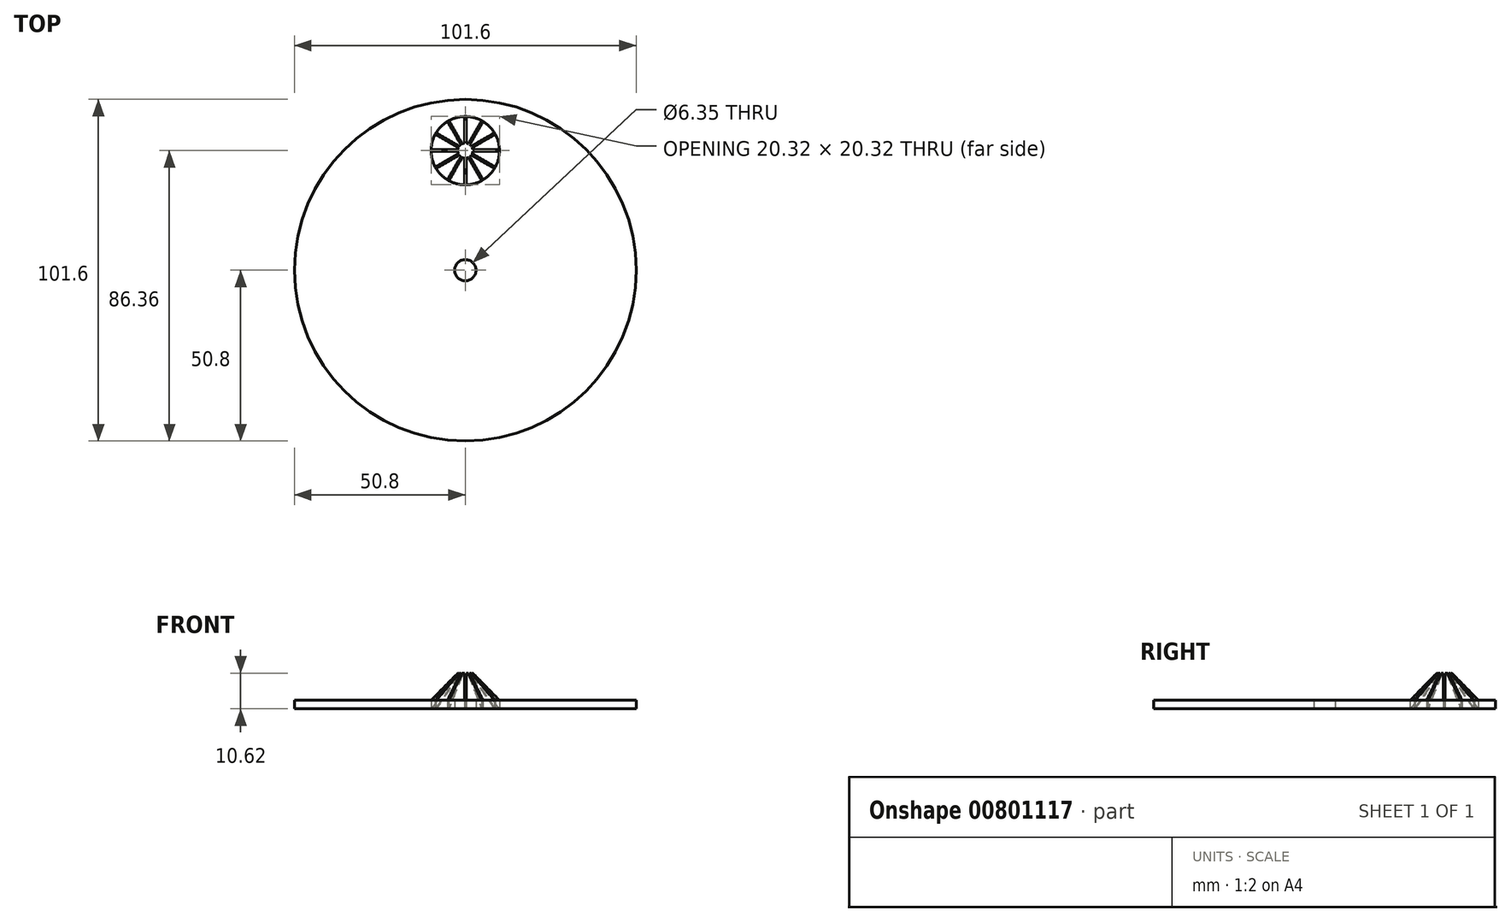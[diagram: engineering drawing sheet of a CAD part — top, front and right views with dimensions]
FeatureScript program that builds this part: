
annotation { "Feature Type Name" : "Feature", "Feature Type Description" : "" }
export const myFeature = defineFeature(function(context is Context, id is Id, definition is map)
    precondition{}
    {
        {
            var Q0;
            Q0=qCreatedBy(makeId("Top.planeOp"),FACE);
            var sketch = newSketch(context, id + "F0", { "sketchPlane" : qUnion([Q0])});
            skCircle(sketch, "E0", {"center": v(0, 0) * mm, "radius": 50.8 * mm});
            skCircle(sketch, "E1", {"center": v(0, 0) * mm, "radius": 3.18 * mm});
            skSolve(sketch);
        }
        {
            var Q0;
            Q0 = qSketchRegion(id + "F0", true);
            extrude(context, id + "F1", {"entities" : qUnion([Q0]), "depth" : 2.54 * mm, "offsetDistance" : 25.4 * mm});
        }
        {
            var Q0;
            Q0=makeQuery(id+"F1.opExtrude","CAP_FACE",FACE,{"disambiguationData":[OSD([sQuery(id+"F0.wireOp",EDGE,"E0"),sQuery(id+"F0.wireOp",EDGE,"E1")])],"isStart":false});
            var sketch = newSketch(context, id + "F2", { "sketchPlane" : qUnion([Q0])});
            skLineSegment(sketch, "E2", {"start": v(0, 0) * mm, "end": v(0, 35.56) * mm, "construction": true});
            skCircle(sketch, "E3", {"center": v(0, 35.56) * mm, "radius": 10.16 * mm});
            skSolve(sketch);
        }
        {
            var Q0;
            Q0=makeQuery(id+"F2.imprint","IMPRINT",FACE,{"disambiguationData":[TD([[makeQuery(id+"F2.imprint","IMPRINT",EDGE,{"derivedFrom":sQuery(id+"F2.wireOp",EDGE,"E3")}),1.0]])]});
            var Q1;
            Q1=sQuery(id+"F2.wireOp",EDGE,"E3");
            extrude(context, id + "F3", {"entities" : qUnion([Q0]), "operationType" : NewBodyOperationType.REMOVE, "surfaceEntities" : qUnion([Q1]), "oppositeDirection" : true, "depth" : 25.4 * mm, "offsetDistance" : 25.4 * mm});
        }
        {
            var Q0;
            Q0=qCreatedBy(makeId("Right.planeOp"),FACE);
            var sketch = newSketch(context, id + "F4", { "sketchPlane" : qUnion([Q0])});
            skLineSegment(sketch, "E4", {"start": v(45.72, 2.54) * mm, "end": v(37.8, 10.62) * mm});
            skLineSegment(sketch, "E5", {"start": v(37.8, 10.62) * mm, "end": v(37.8, 10) * mm});
            skLineSegment(sketch, "E6", {"start": v(37.8, 10) * mm, "end": v(45.72, 0) * mm});
            skLineSegment(sketch, "E7", {"start": v(45.72, 2.54) * mm, "end": v(45.72, 0) * mm});
            skSolve(sketch);
        }
        {
            var Q0;
            Q0=makeQuery(id+"F4.imprint","IMPRINT",FACE,{"disambiguationData":[TD([[makeQuery(id+"F4.imprint","IMPRINT",EDGE,{"derivedFrom":sQuery(id+"F4.wireOp",EDGE,"E4")}),1.0]])]});
            var Q1;
            Q1=sQuery(id+"F2.wireOp",EDGE,"E3");
            revolve(context, id + "F5", {"operationType" : NewBodyOperationType.ADD, "surfaceOperationType" : NewSurfaceOperationType.NEW, "entities" : qUnion([Q0]), "axis" : qUnion([Q1]), "revolveType" : RevolveType.FULL});
        }
        {
            var Q0;
            Q0=makeQuery(id+"F1.opExtrude","CAP_FACE",FACE,{"disambiguationData":[OSD([sQuery(id+"F0.wireOp",EDGE,"E0"),sQuery(id+"F0.wireOp",EDGE,"E1")])],"isStart":true});
            var sketch = newSketch(context, id + "F6", { "sketchPlane" : qUnion([Q0])});
            skLineSegment(sketch, "E8.bottom", {"start": v(0, -35.81) * mm, "end": v(10.16, -35.81) * mm});
            skLineSegment(sketch, "E8.top", {"start": v(0, -35.3) * mm, "end": v(10.16, -35.3) * mm});
            skLineSegment(sketch, "E8.left", {"start": v(0, -35.81) * mm, "end": v(0, -35.3) * mm});
            skLineSegment(sketch, "E8.right", {"start": v(10.16, -35.81) * mm, "end": v(10.16, -35.3) * mm});
            skPoint(sketch, "E9", {"position": v(0, -35.56) * mm});
            skLineSegment(sketch, "E10.1.0", {"start": v(-0.13, -35.34) * mm, "end": v(8.67, -30.26) * mm});
            skLineSegment(sketch, "E10.1.1", {"start": v(8.93, -30.7) * mm, "end": v(8.67, -30.26) * mm});
            skLineSegment(sketch, "E10.1.2", {"start": v(0.13, -35.78) * mm, "end": v(8.93, -30.7) * mm});
            skLineSegment(sketch, "E10.2.0", {"start": v(-0.22, -35.43) * mm, "end": v(4.86, -26.63) * mm});
            skLineSegment(sketch, "E10.2.1", {"start": v(5.3, -26.89) * mm, "end": v(4.86, -26.63) * mm});
            skLineSegment(sketch, "E10.2.2", {"start": v(0.22, -35.69) * mm, "end": v(5.3, -26.89) * mm});
            skLineSegment(sketch, "E10.3.0", {"start": v(-0.25, -35.56) * mm, "end": v(-0.25, -25.4) * mm});
            skLineSegment(sketch, "E10.3.1", {"start": v(0.25, -25.4) * mm, "end": v(-0.25, -25.4) * mm});
            skLineSegment(sketch, "E10.3.2", {"start": v(0.25, -35.56) * mm, "end": v(0.25, -25.4) * mm});
            skLineSegment(sketch, "E10.4.0", {"start": v(-0.22, -35.69) * mm, "end": v(-5.3, -26.89) * mm});
            skLineSegment(sketch, "E10.4.1", {"start": v(-4.86, -26.63) * mm, "end": v(-5.3, -26.89) * mm});
            skLineSegment(sketch, "E10.4.2", {"start": v(0.22, -35.43) * mm, "end": v(-4.86, -26.63) * mm});
            skLineSegment(sketch, "E10.5.0", {"start": v(-0.13, -35.78) * mm, "end": v(-8.93, -30.7) * mm});
            skLineSegment(sketch, "E10.5.1", {"start": v(-8.67, -30.26) * mm, "end": v(-8.93, -30.7) * mm});
            skLineSegment(sketch, "E10.5.2", {"start": v(0.13, -35.34) * mm, "end": v(-8.67, -30.26) * mm});
            skLineSegment(sketch, "E10.6.0", {"start": v(0, -35.81) * mm, "end": v(-10.16, -35.81) * mm});
            skLineSegment(sketch, "E10.6.1", {"start": v(-10.16, -35.3) * mm, "end": v(-10.16, -35.81) * mm});
            skLineSegment(sketch, "E10.6.2", {"start": v(0, -35.3) * mm, "end": v(-10.16, -35.3) * mm});
            skLineSegment(sketch, "E10.7.0", {"start": v(0.13, -35.78) * mm, "end": v(-8.67, -40.86) * mm});
            skLineSegment(sketch, "E10.7.1", {"start": v(-8.93, -40.42) * mm, "end": v(-8.67, -40.86) * mm});
            skLineSegment(sketch, "E10.7.2", {"start": v(-0.13, -35.34) * mm, "end": v(-8.93, -40.42) * mm});
            skLineSegment(sketch, "E10.8.0", {"start": v(0.22, -35.69) * mm, "end": v(-4.86, -44.49) * mm});
            skLineSegment(sketch, "E10.8.1", {"start": v(-5.3, -44.23) * mm, "end": v(-4.86, -44.49) * mm});
            skLineSegment(sketch, "E10.8.2", {"start": v(-0.22, -35.43) * mm, "end": v(-5.3, -44.23) * mm});
            skLineSegment(sketch, "E10.9.0", {"start": v(0.25, -35.56) * mm, "end": v(0.25, -45.72) * mm});
            skLineSegment(sketch, "E10.9.1", {"start": v(-0.25, -45.72) * mm, "end": v(0.25, -45.72) * mm});
            skLineSegment(sketch, "E10.9.2", {"start": v(-0.25, -35.56) * mm, "end": v(-0.25, -45.72) * mm});
            skLineSegment(sketch, "E11.2.10.0", {"start": v(0.22, -35.43) * mm, "end": v(5.3, -44.23) * mm});
            skLineSegment(sketch, "E11.3.10.0", {"start": v(4.86, -44.49) * mm, "end": v(5.3, -44.23) * mm});
            skLineSegment(sketch, "E11.6.10.0", {"start": v(-0.22, -35.69) * mm, "end": v(4.86, -44.49) * mm});
            skLineSegment(sketch, "E11.2.11.0", {"start": v(0.13, -35.34) * mm, "end": v(8.93, -40.42) * mm});
            skLineSegment(sketch, "E11.3.11.0", {"start": v(8.67, -40.86) * mm, "end": v(8.93, -40.42) * mm});
            skLineSegment(sketch, "E11.6.11.0", {"start": v(-0.13, -35.78) * mm, "end": v(8.67, -40.86) * mm});
            skSolve(sketch);
        }
        {
            var Q0;
            Q0 = qSketchRegion(id + "F6", true);
            extrude(context, id + "F7", {"entities" : qUnion([Q0]), "operationType" : NewBodyOperationType.REMOVE, "oppositeDirection" : true, "depth" : 25.4 * mm, "offsetDistance" : 25.4 * mm});
        }
    });
